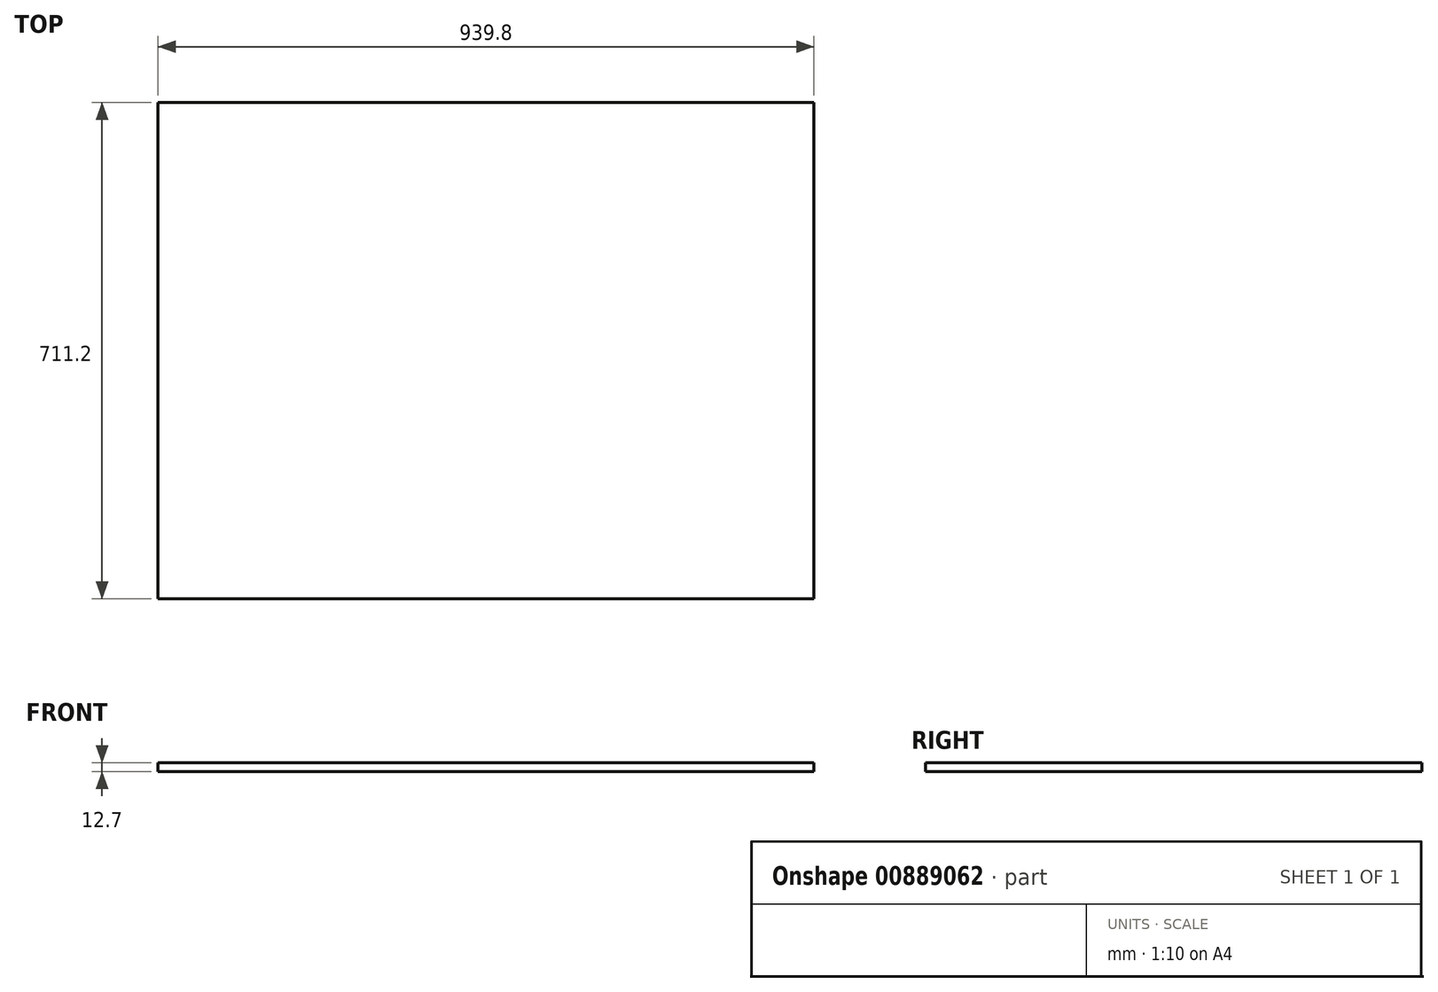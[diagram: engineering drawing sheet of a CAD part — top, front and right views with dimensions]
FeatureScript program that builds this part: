
annotation { "Feature Type Name" : "Feature", "Feature Type Description" : "" }
export const myFeature = defineFeature(function(context is Context, id is Id, definition is map)
    precondition{}
    {
        {
            var Q0;
            Q0=qCreatedBy(makeId("Top.planeOp"),FACE);
            var sketch = newSketch(context, id + "F0", { "sketchPlane" : qUnion([Q0])});
            skLineSegment(sketch, "E0.bottom", {"start": v(-469.9, 355.6) * mm, "end": v(469.9, 355.6) * mm});
            skLineSegment(sketch, "E0.top", {"start": v(-469.9, -355.6) * mm, "end": v(469.9, -355.6) * mm});
            skLineSegment(sketch, "E0.left", {"start": v(-469.9, 355.6) * mm, "end": v(-469.9, -355.6) * mm});
            skLineSegment(sketch, "E0.right", {"start": v(469.9, 355.6) * mm, "end": v(469.9, -355.6) * mm});
            skPoint(sketch, "E0.middle", {"position": v(0, 0) * mm});
            skSolve(sketch);
        }
        {
            var Q0;
            Q0 = qSketchRegion(id + "F0", true);
            extrude(context, id + "F1", {"entities" : qUnion([Q0]), "depth" : 12.7 * mm, "offsetDistance" : 25.4 * mm});
        }
    });
